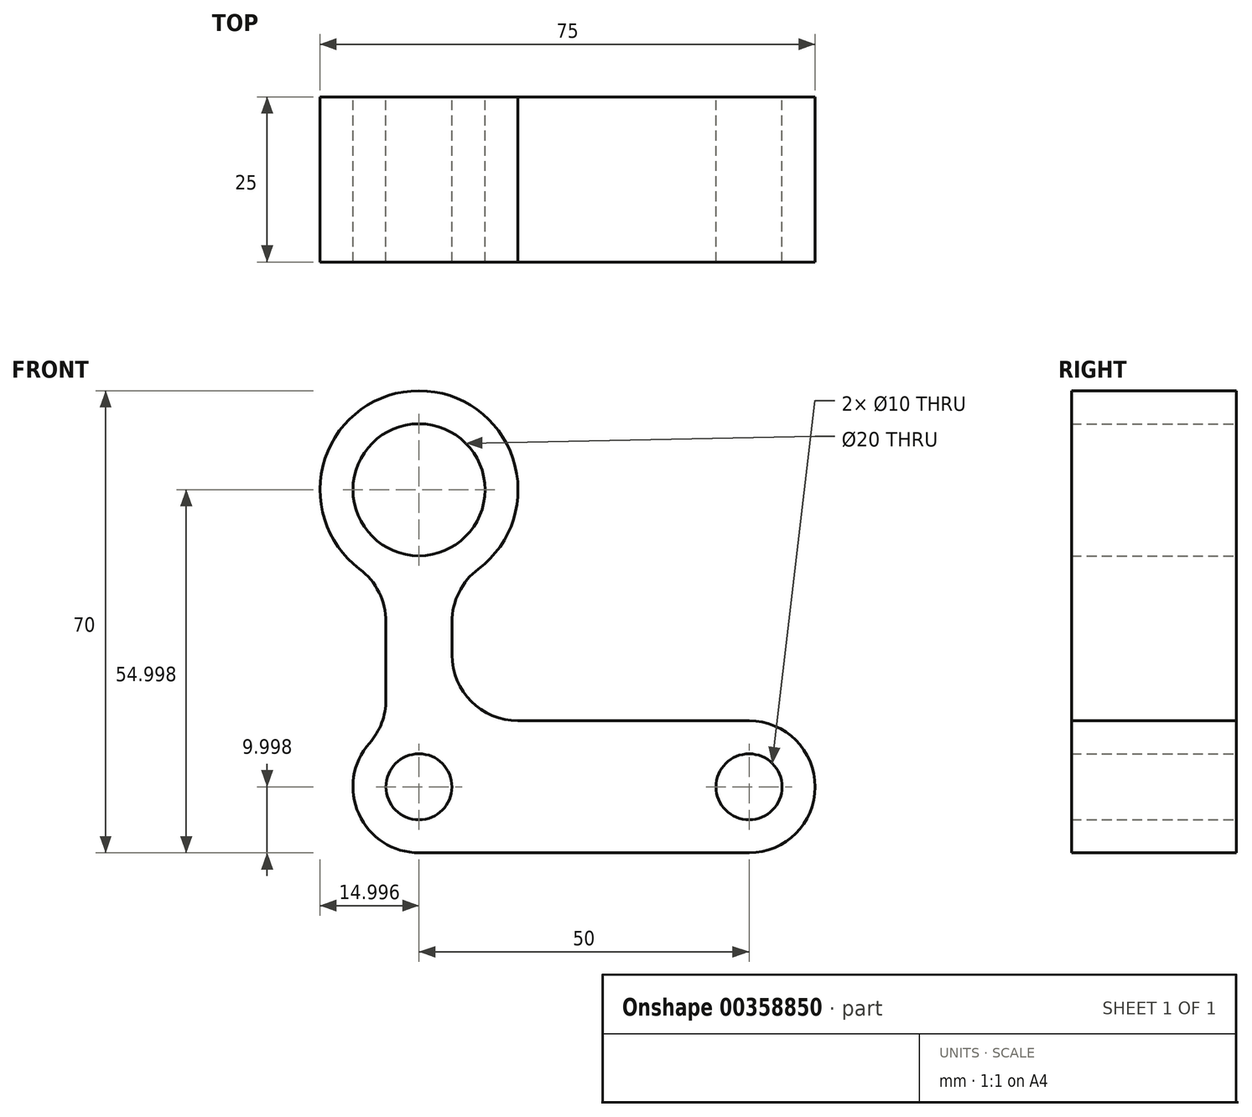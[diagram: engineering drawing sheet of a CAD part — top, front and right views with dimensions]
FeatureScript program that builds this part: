
annotation { "Feature Type Name" : "Feature", "Feature Type Description" : "" }
export const myFeature = defineFeature(function(context is Context, id is Id, definition is map)
    precondition{}
    {
        {
            var Q0;
            Q0=qCreatedBy(makeId("Front.planeOp"),FACE);
            var sketch = newSketch(context, id + "F0", { "sketchPlane" : qUnion([Q0])});
            skLineSegment(sketch, "E0", {"start": v(-35.41, -28.02) * mm, "end": v(14.59, -28.02) * mm});
            skLineSegment(sketch, "E1", {"start": v(24.59, -18.02) * mm, "end": v(24.59, -18.02) * mm});
            skLineSegment(sketch, "E2", {"start": v(14.59, -8.02) * mm, "end": v(-11.11, -8.02) * mm});
            skPoint(sketch, "E3.visualSharp", {"position": v(24.59, -8.02) * mm});
            skArc(sketch, "E3.filletArc", {"start": v(24.59, -18.02) * mm, "mid": v(21.66, -10.95) * mm, "end": v(14.59, -8.02) * mm});
            skPoint(sketch, "E4.visualSharp", {"position": v(24.59, -28.02) * mm});
            skArc(sketch, "E4.filletArc", {"start": v(14.59, -28.02) * mm, "mid": v(21.66, -25.1) * mm, "end": v(24.59, -18.02) * mm});
            skCircle(sketch, "E5", {"center": v(14.59, -18.02) * mm, "radius": 5 * mm});
            skCircle(sketch, "E6", {"center": v(-35.41, -18.02) * mm, "radius": 5 * mm});
            skLineSegment(sketch, "E7", {"start": v(-45.41, -18.02) * mm, "end": v(-45.41, -18.02) * mm});
            skPoint(sketch, "E8.visualSharp", {"position": v(-45.41, -28.02) * mm});
            skArc(sketch, "E8.filletArc", {"start": v(-45.41, -18.02) * mm, "mid": v(-42.49, -25.1) * mm, "end": v(-35.41, -28.02) * mm});
            skLineSegment(sketch, "E9", {"start": v(-35.41, -8.02) * mm, "end": v(-35.41, -8.02) * mm});
            skPoint(sketch, "E10.visualSharp", {"position": v(-45.41, -8.02) * mm});
            skArc(sketch, "E11", {"start": v(-42.91, -11.4) * mm, "mid": v(-44.77, -14.49) * mm, "end": v(-45.41, -18.02) * mm});
            skLineSegment(sketch, "E12", {"start": v(-20.41, -8.02) * mm, "end": v(-11.11, -8.02) * mm});
            skPoint(sketch, "E13.start.orphan", {"position": v(-30.41, -18.02) * mm});
            skPoint(sketch, "E14.visualSharp", {"position": v(-30.41, -8.02) * mm});
            skLineSegment(sketch, "E15", {"start": v(-40.41, 6.98) * mm, "end": v(-40.41, -4.8) * mm});
            skCircle(sketch, "E16", {"center": v(-35.41, 26.98) * mm, "radius": 10 * mm});
            skArc(sketch, "E17", {"start": v(-26.41, 14.98) * mm, "mid": v(-35.41, 41.98) * mm, "end": v(-44.41, 14.98) * mm});
            skLineSegment(sketch, "E18", {"start": v(-20.41, -8.02) * mm, "end": v(-20.41, -8.02) * mm});
            skLineSegment(sketch, "E19", {"start": v(-30.41, 1.98) * mm, "end": v(-30.41, 1.98) * mm});
            skLineSegment(sketch, "E20", {"start": v(-30.41, 1.98) * mm, "end": v(-30.41, 6.98) * mm});
            skPoint(sketch, "E21.visualSharp", {"position": v(-30.41, 16.98) * mm});
            skArc(sketch, "E21.filletArc", {"start": v(-26.41, 14.98) * mm, "mid": v(-29.36, 11.45) * mm, "end": v(-30.41, 6.98) * mm});
            skArc(sketch, "E22.filletArc", {"start": v(-30.41, 1.98) * mm, "mid": v(-27.49, -5.1) * mm, "end": v(-20.41, -8.02) * mm});
            skPoint(sketch, "E23.visualSharp", {"position": v(-40.41, -9.36) * mm});
            skArc(sketch, "E23.filletArc", {"start": v(-42.91, -11.4) * mm, "mid": v(-41.06, -8.33) * mm, "end": v(-40.41, -4.8) * mm});
            skLineSegment(sketch, "E24", {"start": v(-40.41, 6.98) * mm, "end": v(-40.41, 6.98) * mm});
            skPoint(sketch, "E25.visualSharp", {"position": v(-40.41, 16.98) * mm});
            skArc(sketch, "E25.filletArc", {"start": v(-40.41, 6.98) * mm, "mid": v(-41.47, 11.45) * mm, "end": v(-44.41, 14.98) * mm});
            skSolve(sketch);
        }
        {
            var Q0;
            Q0=makeQuery(id+"F0.imprint","IMPRINT",FACE,{"disambiguationData":[TD([[makeQuery(id+"F0.imprint","IMPRINT",EDGE,{"derivedFrom":sQuery(id+"F0.wireOp",EDGE,"E0")}),1.0]])]});
            extrude(context, id + "F1", {"entities" : qUnion([Q0]), "depth" : 25 * mm});
        }
    });
